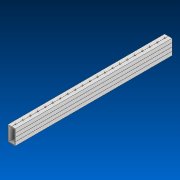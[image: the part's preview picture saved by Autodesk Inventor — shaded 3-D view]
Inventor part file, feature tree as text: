
AUTODESK INVENTOR PART (.ipt)
format: ipt  version: 2022.2 (Build 262287000, 287)  size: 482,816 bytes
history: native  units: in
note: dims shown in document units (in); Inventor stores cm internally (conversion verified against a paired STEP export)
features: other x22, extrude x1, pattern_linear x1, sketch x1
ambient origin geometry x8: Origin, YZ Plane, XZ Plane, XY Plane, X Axis, Y Axis, Z Axis, Center Point
bodies: Solid1 (feature_tree)
feature tree (25):
  extrude  "Extrusion1"  Depth=2.0in
  other  "Work Axis1"
  pattern_linear  "Rectangular Pattern1"  Spacing1=38.0in  [1 undecoded]
  sketch  "Sketch1"  dims[d0=1.0in d1=2.0in d2=38.0in d3=0.0in d4=8.2677in d6=1.0in]
  other  "Work Axis2"
  other  "Work Axis3"
  other  "Work Axis4"
  other  "Work Axis5"
  other  "Work Axis6"
  other  "Work Axis7"
  other  "Work Axis8"
  other  "Work Axis9"
  other  "Work Axis10"
  other  "Work Axis60"
  other  "Work Axis61"
  other  "Work Axis62"
  other  "Work Axis63"
  other  "Work Axis64"
  other  "Work Axis65"
  other  "Work Axis66"
  other  "Work Axis67"
  other  "Work Axis68"
  other  "Work Axis69"
  other  "Work Axis70"
  other  "Cut-Extrude2"
note: 1 required parameter value undecoded (feature->parameter linkage not recoverable at this tier; creation-order binding heuristic only, values carry confidence <= 0.55)
